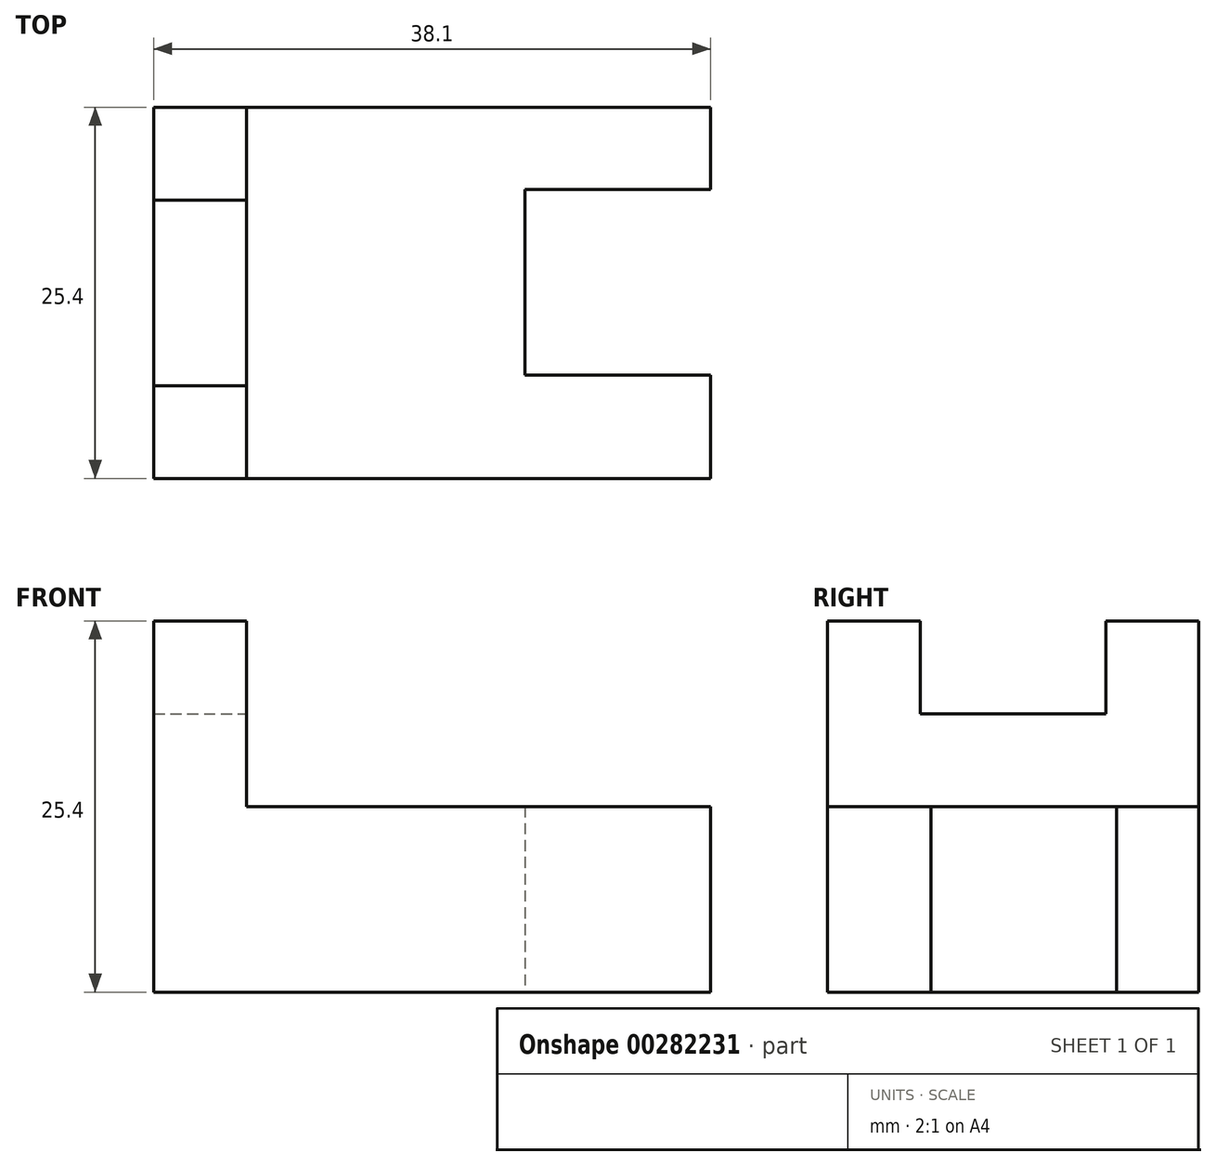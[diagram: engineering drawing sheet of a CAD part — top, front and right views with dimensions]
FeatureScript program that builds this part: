
annotation { "Feature Type Name" : "Feature", "Feature Type Description" : "" }
export const myFeature = defineFeature(function(context is Context, id is Id, definition is map)
    precondition{}
    {
        {
            var Q0;
            Q0=qCreatedBy(makeId("Top.planeOp"),FACE);
            var sketch = newSketch(context, id + "F0", { "sketchPlane" : qUnion([Q0])});
            skLineSegment(sketch, "E0.bottom", {"start": v(0, 0) * mm, "end": v(38.1, 0) * mm});
            skLineSegment(sketch, "E0.top", {"start": v(0, 25.4) * mm, "end": v(38.1, 25.4) * mm});
            skLineSegment(sketch, "E0.left", {"start": v(0, 0) * mm, "end": v(0, 25.4) * mm});
            skLineSegment(sketch, "E0.right", {"start": v(38.1, 0) * mm, "end": v(38.1, 25.4) * mm});
            skLineSegment(sketch, "E1.bottom", {"start": v(38.1, 19.78) * mm, "end": v(25.4, 19.78) * mm});
            skLineSegment(sketch, "E1.top", {"start": v(38.1, 7.08) * mm, "end": v(25.4, 7.08) * mm});
            skLineSegment(sketch, "E1.left", {"start": v(38.1, 19.78) * mm, "end": v(38.1, 7.08) * mm});
            skLineSegment(sketch, "E1.right", {"start": v(25.4, 19.78) * mm, "end": v(25.4, 7.08) * mm});
            skSolve(sketch);
        }
        {
            var Q0;
            {var subQ1=sQuery(id+"F0.wireOp",EDGE,"E0.bottom");Q0=makeQuery(id+"F0.imprint","IMPRINT",FACE,{"disambiguationData":[TD([[makeQuery(id+"F0.imprint","IMPRINT",EDGE,{"derivedFrom":subQ1}),1.0]])]});}
            extrude(context, id + "F1", {"entities" : qUnion([Q0]), "depth" : 12.7 * mm});
        }
        {
            var Q0;
            Q0=makeQuery(id+"F1.opExtrude","CAP_FACE",FACE,{"disambiguationData":[OSD([sQuery(id+"F0.wireOp",EDGE,"E0.bottom"),sQuery(id+"F0.wireOp",EDGE,"E0.top"),sQuery(id+"F0.wireOp",EDGE,"E0.left"),sQuery(id+"F0.wireOp",EDGE,"E0.right"),sQuery(id+"F0.wireOp",EDGE,"E1.bottom"),sQuery(id+"F0.wireOp",EDGE,"E1.top"),sQuery(id+"F0.wireOp",EDGE,"E1.right")])],"isStart":false});
            var sketch = newSketch(context, id + "F2", { "sketchPlane" : qUnion([Q0])});
            skLineSegment(sketch, "E2.bottom", {"start": v(0, 0) * mm, "end": v(6.35, 0) * mm});
            skLineSegment(sketch, "E2.top", {"start": v(0, 6.35) * mm, "end": v(6.35, 6.35) * mm});
            skLineSegment(sketch, "E2.left", {"start": v(0, 0) * mm, "end": v(0, 6.35) * mm});
            skLineSegment(sketch, "E2.right", {"start": v(6.35, 0) * mm, "end": v(6.35, 6.35) * mm});
            skLineSegment(sketch, "E3.bottom", {"start": v(0, 25.4) * mm, "end": v(6.35, 25.4) * mm});
            skLineSegment(sketch, "E3.top", {"start": v(0, 19.05) * mm, "end": v(6.35, 19.05) * mm});
            skLineSegment(sketch, "E3.left", {"start": v(0, 25.4) * mm, "end": v(0, 19.05) * mm});
            skLineSegment(sketch, "E3.right", {"start": v(6.35, 25.4) * mm, "end": v(6.35, 19.05) * mm});
            skLineSegment(sketch, "E4.left", {"start": v(0, 19.05) * mm, "end": v(0, 6.35) * mm});
            skLineSegment(sketch, "E4.right", {"start": v(6.35, 19.05) * mm, "end": v(6.35, 6.35) * mm});
            skSolve(sketch);
        }
        {
            var Q0;
            Q0=makeQuery(id+"F2.imprint","IMPRINT",FACE,{"disambiguationData":[TD([[makeQuery(id+"F2.imprint","IMPRINT",EDGE,{"derivedFrom":sQuery(id+"F2.wireOp",EDGE,"E2.bottom")}),1.0]])]});
            var Q1;
            Q1=makeQuery(id+"F2.imprint","IMPRINT",FACE,{"disambiguationData":[TD([[makeQuery(id+"F2.imprint","IMPRINT",EDGE,{"derivedFrom":sQuery(id+"F2.wireOp",EDGE,"E3.bottom")}),-1.0]])]});
            extrude(context, id + "F3", {"entities" : qUnion([Q0, Q1]), "operationType" : NewBodyOperationType.ADD, "depth" : 12.7 * mm});
        }
        {
            var Q0;
            Q0=makeQuery(id+"F1.opExtrude","CAP_FACE",FACE,{"disambiguationData":[OSD([sQuery(id+"F0.wireOp",EDGE,"E0.bottom"),sQuery(id+"F0.wireOp",EDGE,"E0.top"),sQuery(id+"F0.wireOp",EDGE,"E0.left"),sQuery(id+"F0.wireOp",EDGE,"E0.right"),sQuery(id+"F0.wireOp",EDGE,"E1.bottom"),sQuery(id+"F0.wireOp",EDGE,"E1.top"),sQuery(id+"F0.wireOp",EDGE,"E1.right")])],"isStart":false});
            var sketch = newSketch(context, id + "F4", { "sketchPlane" : qUnion([Q0])});
            skLineSegment(sketch, "E5.bottom", {"start": v(0, 19.05) * mm, "end": v(6.35, 19.05) * mm});
            skLineSegment(sketch, "E5.top", {"start": v(0, 6.35) * mm, "end": v(6.35, 6.35) * mm});
            skLineSegment(sketch, "E5.left", {"start": v(0, 19.05) * mm, "end": v(0, 6.35) * mm});
            skLineSegment(sketch, "E5.right", {"start": v(6.35, 19.05) * mm, "end": v(6.35, 6.35) * mm});
            skSolve(sketch);
        }
        {
            var Q0;
            Q0 = qSketchRegion(id + "F4", true);
            extrude(context, id + "F5", {"entities" : qUnion([Q0]), "operationType" : NewBodyOperationType.ADD, "depth" : 6.35 * mm});
        }
    });
